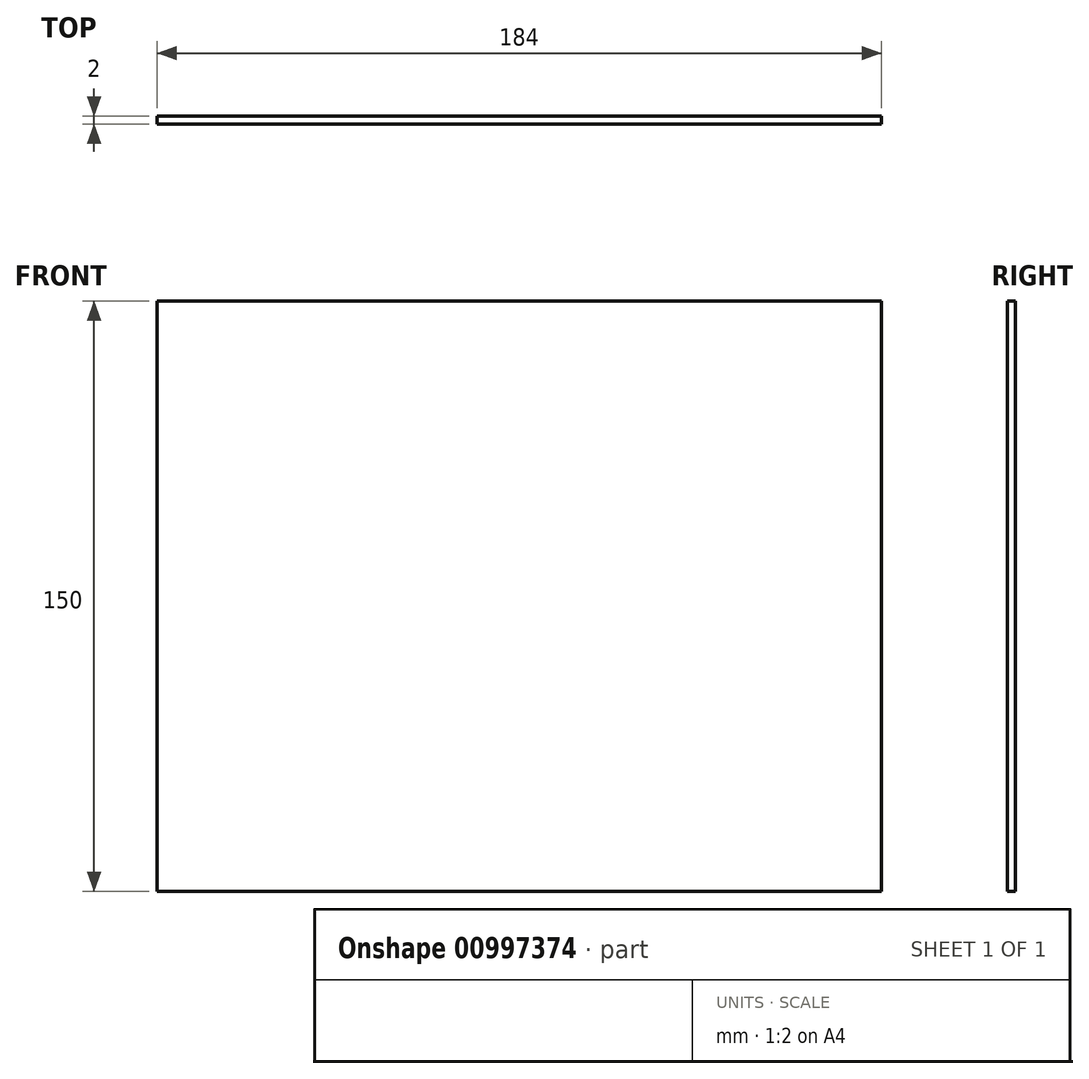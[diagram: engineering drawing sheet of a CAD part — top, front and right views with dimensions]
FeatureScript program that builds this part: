
annotation { "Feature Type Name" : "Feature", "Feature Type Description" : "" }
export const myFeature = defineFeature(function(context is Context, id is Id, definition is map)
    precondition{}
    {
        {
            var Q0;
            Q0=qCreatedBy(makeId("Front.planeOp"),FACE);
            var sketch = newSketch(context, id + "F0", { "sketchPlane" : qUnion([Q0])});
            skLineSegment(sketch, "E0.bottom", {"start": v(92, -75) * mm, "end": v(-92, -75) * mm});
            skLineSegment(sketch, "E0.top", {"start": v(92, 75) * mm, "end": v(-92, 75) * mm});
            skLineSegment(sketch, "E0.left", {"start": v(92, -75) * mm, "end": v(92, 75) * mm});
            skLineSegment(sketch, "E0.right", {"start": v(-92, -75) * mm, "end": v(-92, 75) * mm});
            skPoint(sketch, "E0.middle", {"position": v(0, 0) * mm});
            skSolve(sketch);
        }
        {
            var Q0;
            Q0=makeQuery(id+"F0.imprint","IMPRINT",FACE,{"disambiguationData":[TD([[makeQuery(id+"F0.imprint","IMPRINT",EDGE,{"derivedFrom":sQuery(id+"F0.wireOp",EDGE,"E0.bottom")}),-1.0]])]});
            var Q1;
            Q1=qSketchRegion(id+"F0",true);
            extrude(context, id + "F1", {"entities" : qUnion([Q0, Q1]), "depth" : 2 * mm, "offsetDistance" : 25 * mm});
        }
    });
